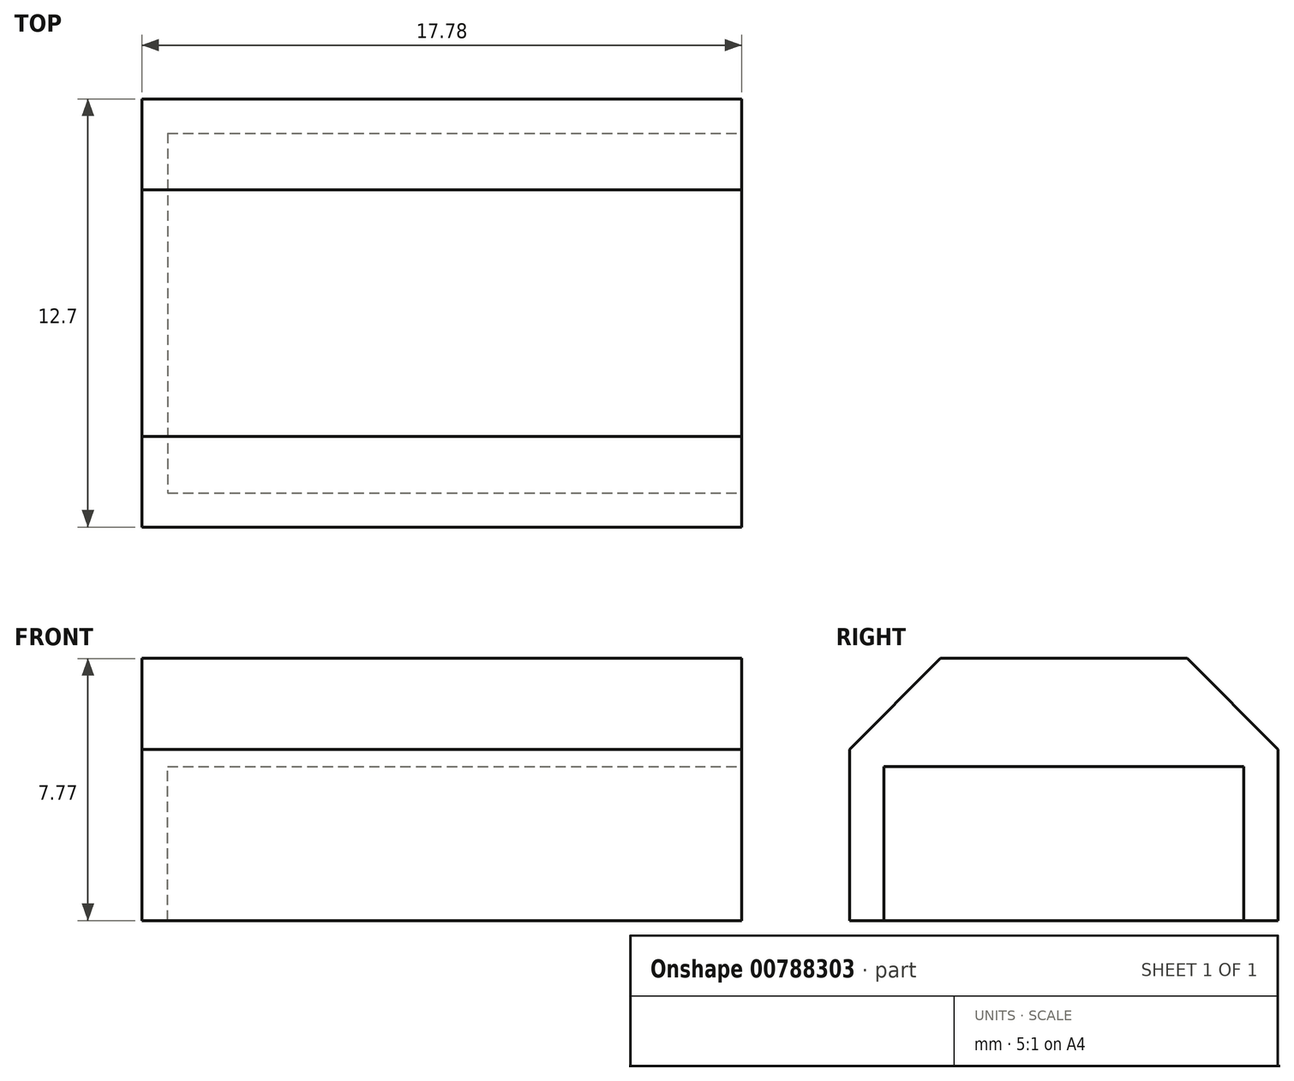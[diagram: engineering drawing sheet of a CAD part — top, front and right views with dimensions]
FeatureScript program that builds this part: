
annotation { "Feature Type Name" : "Feature", "Feature Type Description" : "" }
export const myFeature = defineFeature(function(context is Context, id is Id, definition is map)
    precondition{}
    {
        {
            var Q0;
            Q0=qCreatedBy(makeId("Top.planeOp"),FACE);
            var sketch = newSketch(context, id + "F0", { "sketchPlane" : qUnion([Q0])});
            skLineSegment(sketch, "E0.bottom", {"start": v(8.89, 6.35) * mm, "end": v(-8.9, 6.35) * mm});
            skLineSegment(sketch, "E0.top", {"start": v(8.9, -6.35) * mm, "end": v(-8.9, -6.35) * mm});
            skLineSegment(sketch, "E0.left", {"start": v(8.89, 6.35) * mm, "end": v(8.89, -6.35) * mm});
            skLineSegment(sketch, "E0.right", {"start": v(-8.9, 6.35) * mm, "end": v(-8.9, -6.35) * mm});
            skPoint(sketch, "E0.middle", {"position": v(0, 0) * mm});
            skSolve(sketch);
        }
        {
            var Q0;
            Q0=makeQuery(id+"F0.imprint","IMPRINT",FACE,{"disambiguationData":[TD([[makeQuery(id+"F0.imprint","IMPRINT",EDGE,{"derivedFrom":sQuery(id+"F0.wireOp",EDGE,"E0.bottom")}),1.0]])]});
            extrude(context, id + "F1", {"entities" : qUnion([Q0]), "depth" : 5.08 * mm, "offsetDistance" : 25.4 * mm});
        }
        {
            var Q0;
            Q0=makeQuery(id+"F1.opExtrude","SWEPT_FACE",FACE,{"disambiguationData":[OSD([sQuery(id+"F0.wireOp",EDGE,"E0.left")])]});
            var sketch = newSketch(context, id + "F2", { "sketchPlane" : qUnion([Q0])});
            skLineSegment(sketch, "E1.0.0", {"start": v(-6.35, 0) * mm, "end": v(6.35, 0) * mm});
            skLineSegment(sketch, "E1.0.1", {"start": v(6.35, 0) * mm, "end": v(6.35, 5.08) * mm});
            skLineSegment(sketch, "E1.0.2", {"start": v(6.35, 5.08) * mm, "end": v(-6.35, 5.08) * mm});
            skLineSegment(sketch, "E1.0.3", {"start": v(-6.35, 5.08) * mm, "end": v(-6.35, 0) * mm});
            skLineSegment(sketch, "E2", {"start": v(-6.35, 5.08) * mm, "end": v(-3.66, 7.77) * mm});
            skLineSegment(sketch, "E3", {"start": v(0, -2.4) * mm, "end": v(0, 10.65) * mm, "construction": true});
            skLineSegment(sketch, "E4", {"start": v(-3.66, 7.77) * mm, "end": v(0, 7.77) * mm});
            skLineSegment(sketch, "E5.MirrorCS", {"start": v(3.66, 7.77) * mm, "end": v(0, 7.77) * mm});
            skLineSegment(sketch, "E6.MirrorCS", {"start": v(6.35, 5.08) * mm, "end": v(3.66, 7.77) * mm});
            skSolve(sketch);
        }
        {
            var Q0;
            Q0=makeQuery(id+"F2.imprint","IMPRINT",FACE,{"disambiguationData":[TD([[makeQuery(id+"F2.imprint","IMPRINT",EDGE,{"derivedFrom":sQuery(id+"F2.wireOp",EDGE,"E1.0.2")}),-1.0]])]});
            extrude(context, id + "F3", {"entities" : qUnion([Q0]), "operationType" : NewBodyOperationType.ADD, "oppositeDirection" : true, "depth" : 17.78 * mm, "offsetDistance" : 25.4 * mm});
        }
        {
            var Q0;
            Q0=makeQuery(id+"F3.boolean.opBoolean","MERGE",FACE,{"derivedFrom":[makeQuery(id+"F1.opExtrude","SWEPT_FACE",FACE,{"disambiguationData":[OSD([sQuery(id+"F0.wireOp",EDGE,"E0.left")])]}),makeQuery(id+"F3.opExtrude","CAP_FACE",FACE,{"disambiguationData":[OSD([sQuery(id+"F2.wireOp",EDGE,"E1.0.2"),sQuery(id+"F2.wireOp",EDGE,"E2"),sQuery(id+"F2.wireOp",EDGE,"E4"),sQuery(id+"F2.wireOp",EDGE,"E5.MirrorCS"),sQuery(id+"F2.wireOp",EDGE,"E6.MirrorCS")])],"isStart":true})]});
            var sketch = newSketch(context, id + "F4", { "sketchPlane" : qUnion([Q0])});
            skLineSegment(sketch, "E7", {"start": v(-5.33, 0) * mm, "end": v(-5.33, 4.57) * mm});
            skLineSegment(sketch, "E8", {"start": v(-5.33, 4.57) * mm, "end": v(5.33, 4.57) * mm});
            skLineSegment(sketch, "E9", {"start": v(5.33, 4.57) * mm, "end": v(5.33, 0) * mm});
            skSolve(sketch);
        }
        {
            var Q0;
            {var subQ0=sQuery(id+"F4.wireOp",EDGE,"E7");Q0=makeQuery(id+"F4.imprint","IMPRINT",FACE,{"disambiguationData":[TD([[makeQuery(id+"F4.imprint","IMPRINT",EDGE,{"derivedFrom":subQ0}),-1.0]])]});}
            extrude(context, id + "F5", {"entities" : qUnion([Q0]), "operationType" : NewBodyOperationType.REMOVE, "oppositeDirection" : true, "depth" : 17.02 * mm, "offsetDistance" : 25.4 * mm});
        }
    });
